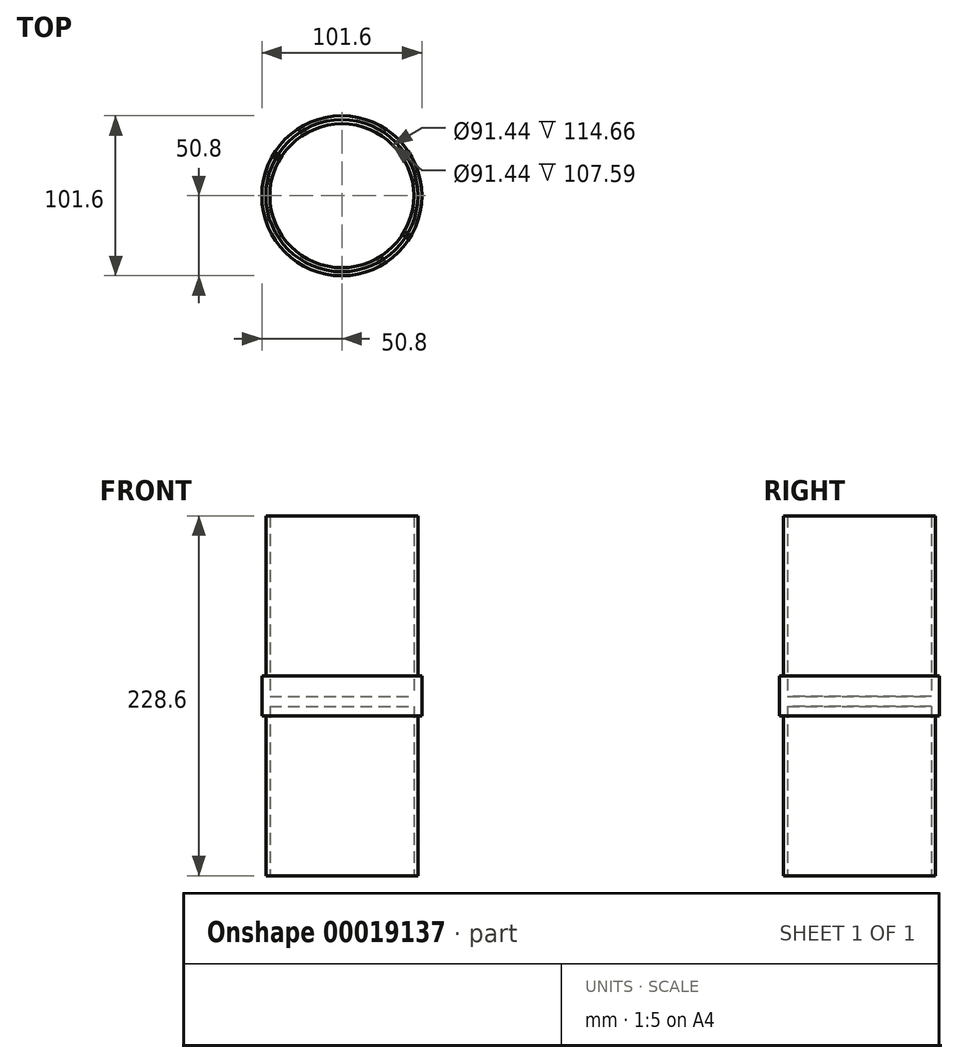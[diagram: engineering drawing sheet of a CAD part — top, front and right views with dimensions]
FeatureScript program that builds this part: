
annotation { "Feature Type Name" : "Feature", "Feature Type Description" : "" }
export const myFeature = defineFeature(function(context is Context, id is Id, definition is map)
    precondition{}
    {
        {
            var Q0;
            Q0=qCreatedBy(makeId("Front.planeOp"),FACE);
            var sketch = newSketch(context, id + "F0", { "sketchPlane" : qUnion([Q0])});
            skLineSegment(sketch, "E0", {"start": v(-48.26, 0) * mm, "end": v(-48.26, 101.6) * mm});
            skLineSegment(sketch, "E1", {"start": v(-48.26, 101.6) * mm, "end": v(-50.8, 101.6) * mm});
            skLineSegment(sketch, "E2", {"start": v(-50.8, 101.6) * mm, "end": v(-50.8, 127) * mm});
            skLineSegment(sketch, "E3", {"start": v(-50.8, 127) * mm, "end": v(-48.26, 127) * mm});
            skLineSegment(sketch, "E4", {"start": v(-48.26, 127) * mm, "end": v(-48.26, 228.6) * mm});
            skLineSegment(sketch, "E5", {"start": v(-48.26, 228.6) * mm, "end": v(-45.72, 228.6) * mm});
            skLineSegment(sketch, "E6", {"start": v(-45.72, 228.6) * mm, "end": v(-45.72, 113.94) * mm});
            skLineSegment(sketch, "E7", {"start": v(-45.72, 0) * mm, "end": v(-48.26, 0) * mm});
            skLineSegment(sketch, "E8", {"start": v(0, 0) * mm, "end": v(0, 138) * mm});
            skLineSegment(sketch, "E9", {"start": v(-45.72, 113.94) * mm, "end": v(0, 113.94) * mm});
            skLineSegment(sketch, "E10", {"start": v(0, 113.94) * mm, "end": v(0, 107.59) * mm});
            skLineSegment(sketch, "E11", {"start": v(0, 107.59) * mm, "end": v(-45.72, 107.59) * mm});
            skLineSegment(sketch, "E12.trimOffspring", {"start": v(-45.72, 107.59) * mm, "end": v(-45.72, 0) * mm});
            skSolve(sketch);
        }
        {
            var Q0;
            Q0=makeQuery(id+"F0.imprint","IMPRINT",FACE,{"disambiguationData":[TD([[makeQuery(id+"F0.imprint","IMPRINT",EDGE,{"derivedFrom":sQuery(id+"F0.wireOp",EDGE,"E0")}),-1.0]])]});
            var Q1;
            Q1=sQuery(id+"F0.wireOp",EDGE,"E8");
            revolve(context, id + "F1", {"entities" : qUnion([Q0]), "axis" : qUnion([Q1]), "revolveType" : RevolveType.FULL});
        }
    });
